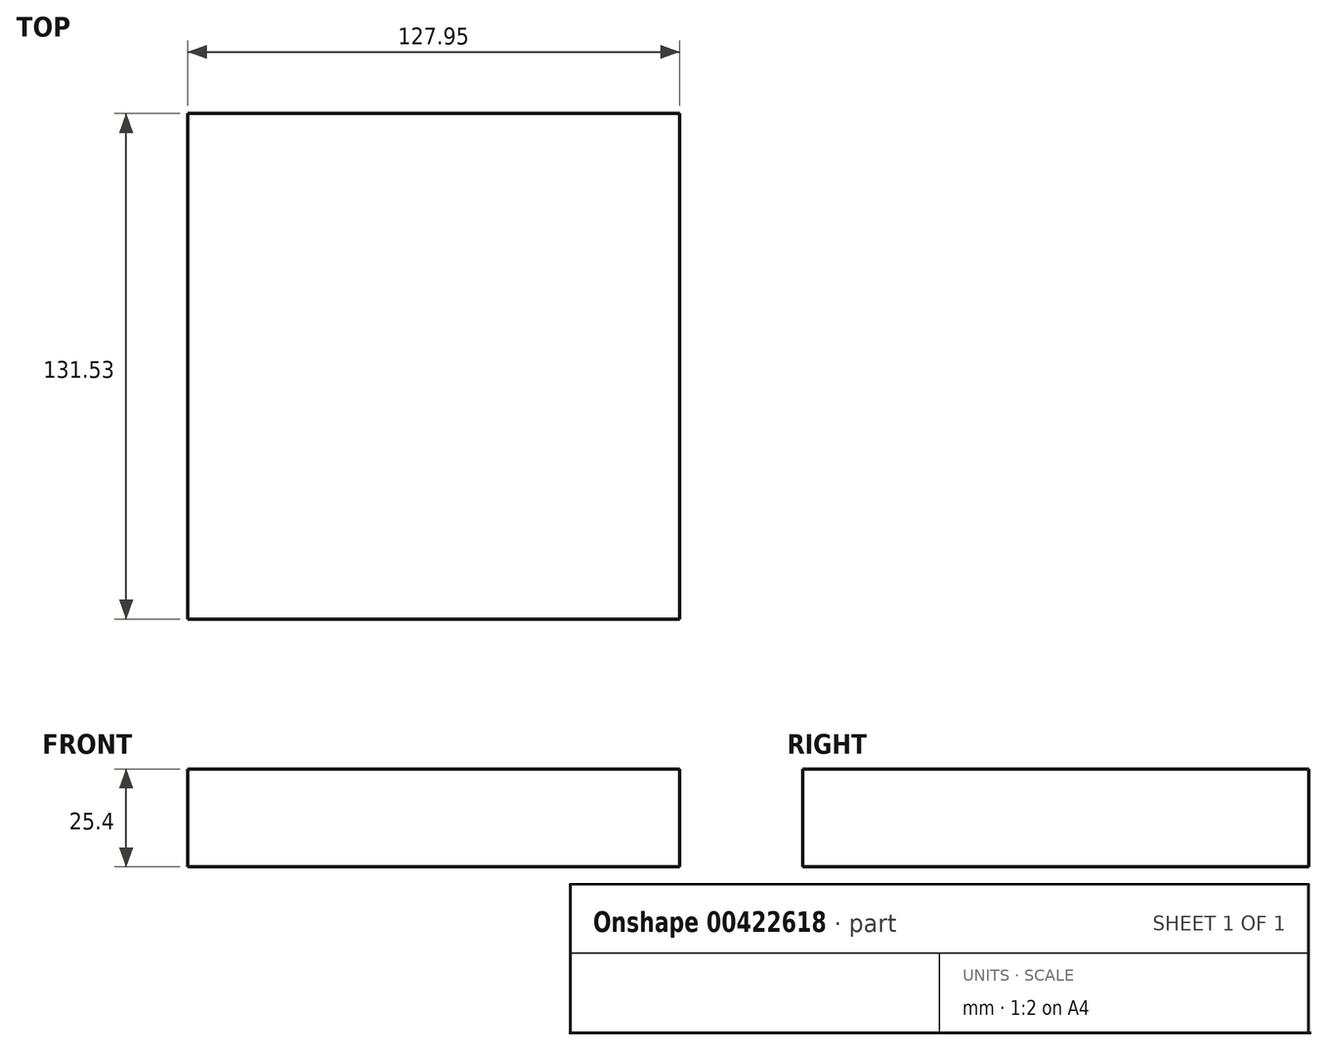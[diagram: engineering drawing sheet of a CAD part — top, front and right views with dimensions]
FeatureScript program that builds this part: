
annotation { "Feature Type Name" : "Feature", "Feature Type Description" : "" }
export const myFeature = defineFeature(function(context is Context, id is Id, definition is map)
    precondition{}
    {
        {
            var Q0;
            Q0=qCreatedBy(makeId("Top.planeOp"),FACE);
            var sketch = newSketch(context, id + "F0", { "sketchPlane" : qUnion([Q0])});
            skLineSegment(sketch, "E0.bottom", {"start": v(0, 0) * mm, "end": v(127.95, 0) * mm});
            skLineSegment(sketch, "E0.top", {"start": v(0, -131.53) * mm, "end": v(127.95, -131.53) * mm});
            skLineSegment(sketch, "E0.left", {"start": v(0, 0) * mm, "end": v(0, -131.53) * mm});
            skLineSegment(sketch, "E0.right", {"start": v(127.95, 0) * mm, "end": v(127.95, -131.53) * mm});
            skSolve(sketch);
        }
        {
            var Q0;
            Q0 = qSketchRegion(id + "F0", true);
            extrude(context, id + "F1", {"entities" : qUnion([Q0]), "depth" : 25.4 * mm});
        }
    });
